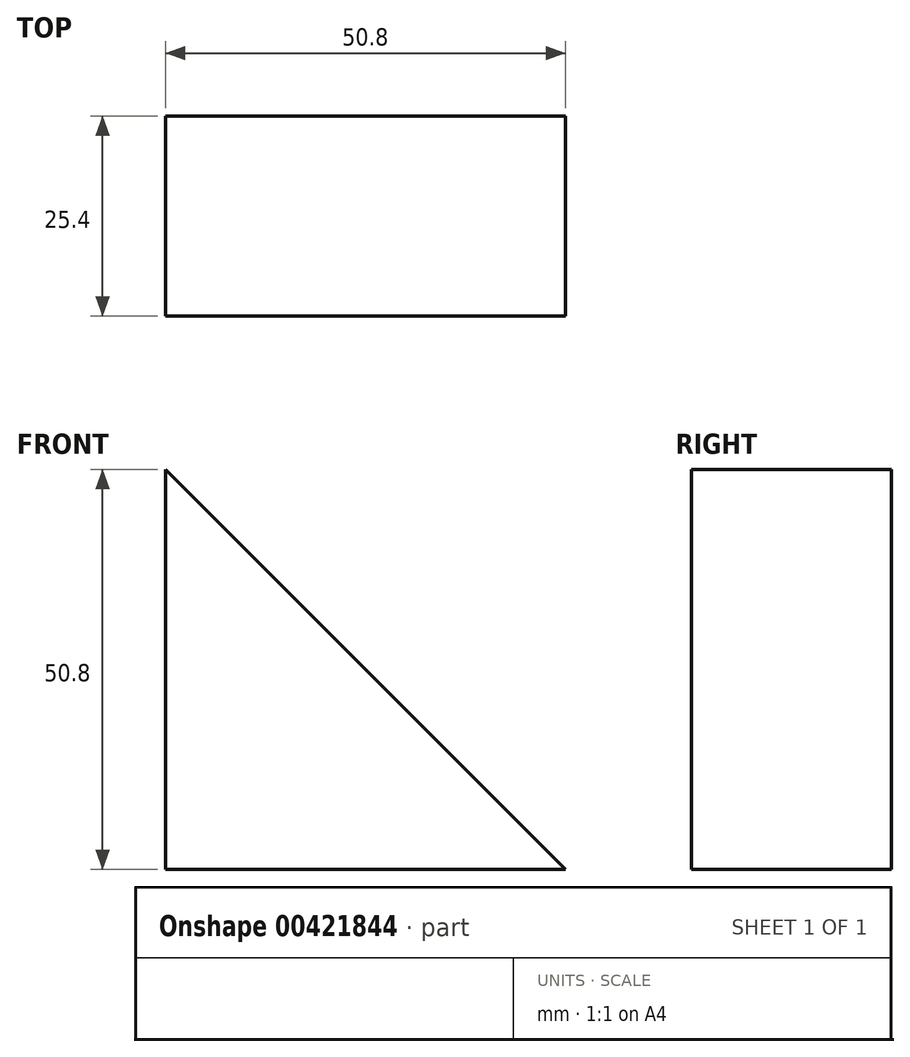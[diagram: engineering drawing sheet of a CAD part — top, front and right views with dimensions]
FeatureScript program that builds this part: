
annotation { "Feature Type Name" : "Feature", "Feature Type Description" : "" }
export const myFeature = defineFeature(function(context is Context, id is Id, definition is map)
    precondition{}
    {
        {
            var Q0;
            Q0=qCreatedBy(makeId("Front.planeOp"),FACE);
            var sketch = newSketch(context, id + "F0", { "sketchPlane" : qUnion([Q0])});
            skLineSegment(sketch, "E0", {"start": v(0, 0) * mm, "end": v(0, 50.8) * mm});
            skLineSegment(sketch, "E1", {"start": v(0, 0) * mm, "end": v(50.8, 0) * mm});
            skLineSegment(sketch, "E2", {"start": v(0, 50.8) * mm, "end": v(50.8, 0) * mm});
            skSolve(sketch);
        }
        {
            var Q0;
            Q0=makeQuery(id+"F0.imprint","IMPRINT",FACE,{"disambiguationData":[TD([[makeQuery(id+"F0.imprint","IMPRINT",EDGE,{"derivedFrom":sQuery(id+"F0.wireOp",EDGE,"E0")}),-1.0]])]});
            extrude(context, id + "F1", {"entities" : qUnion([Q0]), "depth" : 25.4 * mm});
        }
    });
